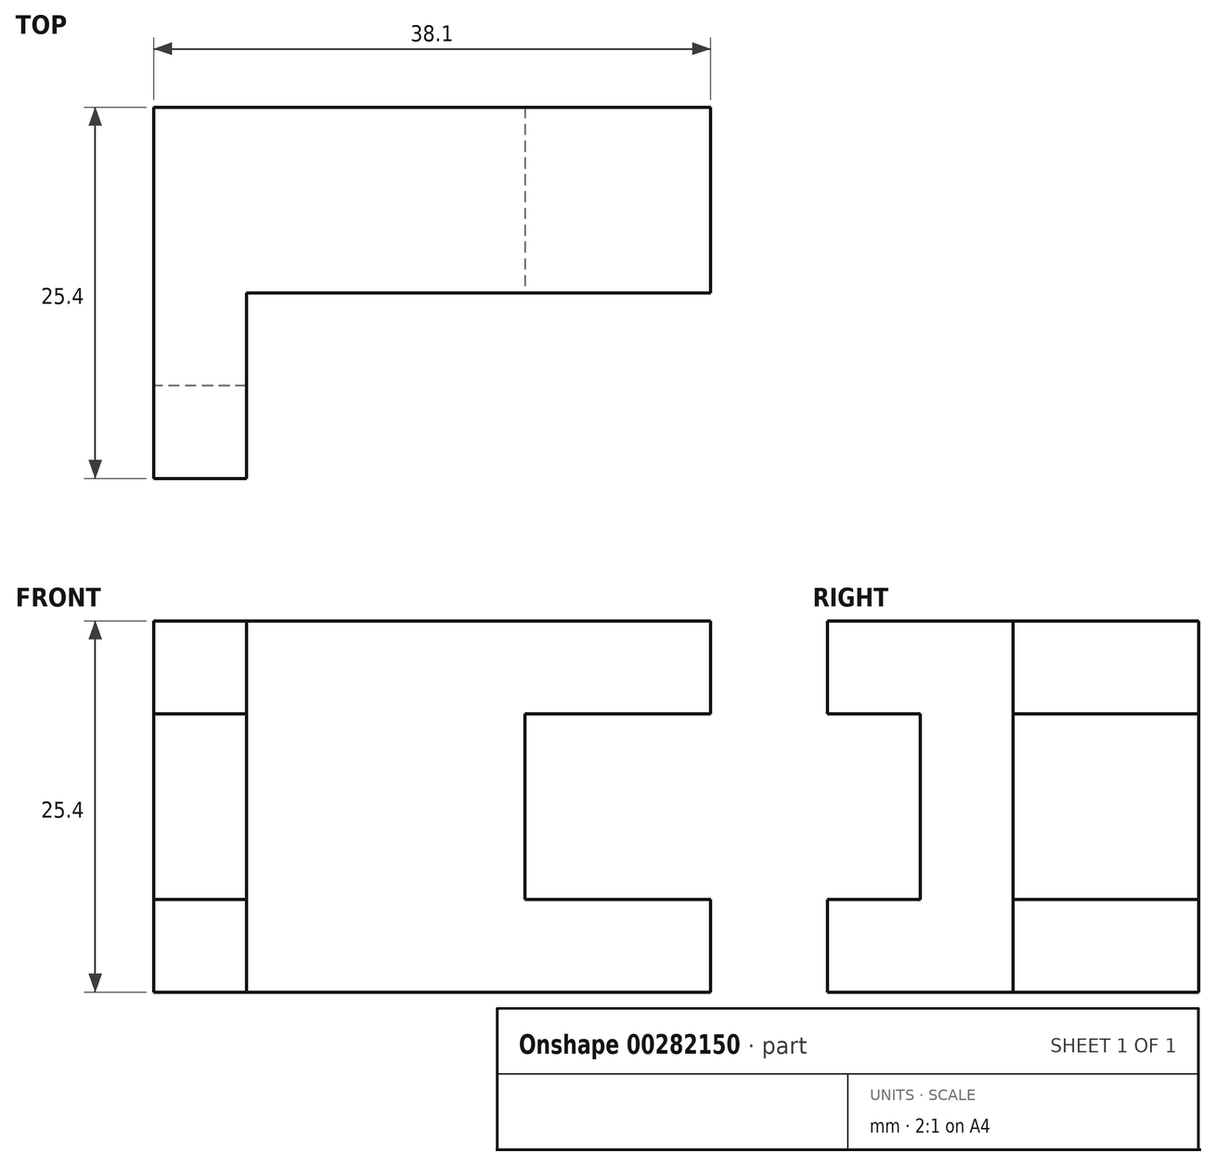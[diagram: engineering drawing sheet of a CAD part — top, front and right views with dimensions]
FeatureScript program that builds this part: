
annotation { "Feature Type Name" : "Feature", "Feature Type Description" : "" }
export const myFeature = defineFeature(function(context is Context, id is Id, definition is map)
    precondition{}
    {
        {
            var Q0;
            Q0=qCreatedBy(makeId("Front.planeOp"),FACE);
            var sketch = newSketch(context, id + "F0", { "sketchPlane" : qUnion([Q0])});
            skLineSegment(sketch, "E0", {"start": v(0, 0) * mm, "end": v(0, 25.4) * mm});
            skLineSegment(sketch, "E1", {"start": v(0, 25.4) * mm, "end": v(25.4, 25.4) * mm});
            skLineSegment(sketch, "E2", {"start": v(25.4, 25.4) * mm, "end": v(25.4, 0) * mm});
            skLineSegment(sketch, "E3", {"start": v(25.4, 0) * mm, "end": v(0, 0) * mm});
            skSolve(sketch);
        }
        {
            var Q0;
            Q0 = qSketchRegion(id + "F0", true);
            extrude(context, id + "F1", {"entities" : qUnion([Q0]), "depth" : 12.7 * mm});
        }
        {
            var Q0;
            Q0=makeQuery(id+"F1.opExtrude","CAP_FACE",FACE,{"disambiguationData":[OSD([sQuery(id+"F0.wireOp",EDGE,"E0"),sQuery(id+"F0.wireOp",EDGE,"E1"),sQuery(id+"F0.wireOp",EDGE,"E2"),sQuery(id+"F0.wireOp",EDGE,"E3")])],"isStart":false});
            var sketch = newSketch(context, id + "F2", { "sketchPlane" : qUnion([Q0])});
            skLineSegment(sketch, "E4", {"start": v(25.4, 25.4) * mm, "end": v(38.1, 25.4) * mm});
            skLineSegment(sketch, "E5", {"start": v(38.1, 25.4) * mm, "end": v(38.1, 19.05) * mm});
            skLineSegment(sketch, "E6", {"start": v(38.1, 19.05) * mm, "end": v(25.4, 19.05) * mm});
            skLineSegment(sketch, "E7", {"start": v(25.4, 0) * mm, "end": v(38.1, 0) * mm});
            skLineSegment(sketch, "E8", {"start": v(38.1, 0) * mm, "end": v(38.1, 6.35) * mm});
            skLineSegment(sketch, "E9", {"start": v(38.1, 6.35) * mm, "end": v(25.4, 6.35) * mm});
            skSolve(sketch);
        }
        {
            var Q0;
            Q0 = qSketchRegion(id + "F2", true);
            var Q1;
            {var subQ0=sQuery(id+"F2.wireOp",EDGE,"E4");Q1=makeQuery(id+"F2.imprint","IMPRINT",FACE,{"disambiguationData":[TD([[makeQuery(id+"F2.imprint","IMPRINT",EDGE,{"derivedFrom":subQ0}),-1.0]])]});}
            var Q2;
            {var subQ0=sQuery(id+"F2.wireOp",EDGE,"E7");Q2=makeQuery(id+"F2.imprint","IMPRINT",FACE,{"disambiguationData":[TD([[makeQuery(id+"F2.imprint","IMPRINT",EDGE,{"derivedFrom":subQ0}),1.0]])]});}
            extrude(context, id + "F3", {"entities" : qUnion([Q0, Q1, Q2]), "operationType" : NewBodyOperationType.ADD, "oppositeDirection" : true, "depth" : 12.7 * mm});
        }
        {
            var Q0;
            Q0=makeQuery(id+"F3.boolean.opBoolean","MERGE",FACE,{"derivedFrom":[makeQuery(id+"F1.opExtrude","SWEPT_FACE",FACE,{"disambiguationData":[OSD([sQuery(id+"F0.wireOp",EDGE,"E3")])]}),makeQuery(id+"F3.opExtrude","SWEPT_FACE",FACE,{"disambiguationData":[OSD([sQuery(id+"F2.wireOp",EDGE,"E7")])]})]});
            var sketch = newSketch(context, id + "F4", { "sketchPlane" : qUnion([Q0])});
            skLineSegment(sketch, "E10", {"start": v(0, 12.7) * mm, "end": v(0, 25.4) * mm});
            skLineSegment(sketch, "E11", {"start": v(0, 25.4) * mm, "end": v(6.35, 25.4) * mm});
            skLineSegment(sketch, "E12", {"start": v(6.35, 25.4) * mm, "end": v(6.35, 12.7) * mm});
            skSolve(sketch);
        }
        {
            var Q0;
            {var subQ0=sQuery(id+"F4.wireOp",EDGE,"E10");Q0=makeQuery(id+"F4.imprint","IMPRINT",FACE,{"disambiguationData":[TD([[makeQuery(id+"F4.imprint","IMPRINT",EDGE,{"derivedFrom":subQ0}),-1.0]])]});}
            extrude(context, id + "F5", {"entities" : qUnion([Q0]), "operationType" : NewBodyOperationType.ADD, "oppositeDirection" : true, "depth" : 6.35 * mm});
        }
        {
            var Q0;
            {var subQ0=sQuery(id+"F0.wireOp",EDGE,"E2");Q0=makeQuery(id+"F3.boolean.opBoolean","MERGE",FACE,{"derivedFrom":[makeQuery(id+"F1.opExtrude","CAP_FACE",FACE,{"disambiguationData":[OSD([sQuery(id+"F0.wireOp",EDGE,"E0"),sQuery(id+"F0.wireOp",EDGE,"E1"),subQ0,sQuery(id+"F0.wireOp",EDGE,"E3")])],"isStart":false}),makeQuery(id+"F3.opExtrude","CAP_FACE",FACE,{"disambiguationData":[OSD([subQ0,sQuery(id+"F2.wireOp",EDGE,"E4"),sQuery(id+"F2.wireOp",EDGE,"E5"),sQuery(id+"F2.wireOp",EDGE,"E6")])],"isStart":true}),makeQuery(id+"F3.opExtrude","CAP_FACE",FACE,{"disambiguationData":[OSD([subQ0,sQuery(id+"F2.wireOp",EDGE,"E7"),sQuery(id+"F2.wireOp",EDGE,"E8"),sQuery(id+"F2.wireOp",EDGE,"E9")])],"isStart":true})]});}
            var sketch = newSketch(context, id + "F6", { "sketchPlane" : qUnion([Q0])});
            skLineSegment(sketch, "E13", {"start": v(6.35, 6.35) * mm, "end": v(6.35, 19.05) * mm});
            skLineSegment(sketch, "E14", {"start": v(6.35, 19.05) * mm, "end": v(0, 19.05) * mm});
            skLineSegment(sketch, "E15", {"start": v(0, 19.05) * mm, "end": v(0, 6.35) * mm});
            skLineSegment(sketch, "E16", {"start": v(6.35, 19.05) * mm, "end": v(6.35, 25.4) * mm});
            skLineSegment(sketch, "E17", {"start": v(6.35, 25.4) * mm, "end": v(0, 25.4) * mm});
            skLineSegment(sketch, "E18", {"start": v(0, 25.4) * mm, "end": v(0, 19.05) * mm});
            skSolve(sketch);
        }
        {
            var Q0;
            Q0 = qSketchRegion(id + "F6", true);
            extrude(context, id + "F7", {"entities" : qUnion([Q0]), "operationType" : NewBodyOperationType.ADD, "depth" : 12.7 * mm});
        }
        {
            var Q0;
            {var subQ0=sQuery(id+"F0.wireOp",EDGE,"E2");Q0=makeQuery(id+"F3.boolean.opBoolean","MERGE",FACE,{"derivedFrom":[makeQuery(id+"F1.opExtrude","CAP_FACE",FACE,{"disambiguationData":[OSD([sQuery(id+"F0.wireOp",EDGE,"E0"),sQuery(id+"F0.wireOp",EDGE,"E1"),subQ0,sQuery(id+"F0.wireOp",EDGE,"E3")])],"isStart":false}),makeQuery(id+"F3.opExtrude","CAP_FACE",FACE,{"disambiguationData":[OSD([subQ0,sQuery(id+"F2.wireOp",EDGE,"E4"),sQuery(id+"F2.wireOp",EDGE,"E5"),sQuery(id+"F2.wireOp",EDGE,"E6")])],"isStart":true}),makeQuery(id+"F3.opExtrude","CAP_FACE",FACE,{"disambiguationData":[OSD([subQ0,sQuery(id+"F2.wireOp",EDGE,"E7"),sQuery(id+"F2.wireOp",EDGE,"E8"),sQuery(id+"F2.wireOp",EDGE,"E9")])],"isStart":true})]});}
            var sketch = newSketch(context, id + "F8", { "sketchPlane" : qUnion([Q0])});
            skLineSegment(sketch, "E19", {"start": v(6.35, 19.05) * mm, "end": v(6.35, 6.35) * mm});
            skLineSegment(sketch, "E20", {"start": v(6.35, 6.35) * mm, "end": v(0, 6.35) * mm});
            skLineSegment(sketch, "E21", {"start": v(0, 6.35) * mm, "end": v(0, 19.05) * mm});
            skLineSegment(sketch, "E22", {"start": v(0, 19.05) * mm, "end": v(6.35, 19.05) * mm});
            skSolve(sketch);
        }
        {
            var Q0;
            Q0=makeQuery(id+"F8.imprint","IMPRINT",FACE,{"disambiguationData":[TD([[makeQuery(id+"F8.imprint","IMPRINT",EDGE,{"derivedFrom":sQuery(id+"F8.wireOp",EDGE,"E19")}),-1.0]])]});
            extrude(context, id + "F9", {"entities" : qUnion([Q0]), "operationType" : NewBodyOperationType.ADD, "depth" : 6.35 * mm});
        }
    });
